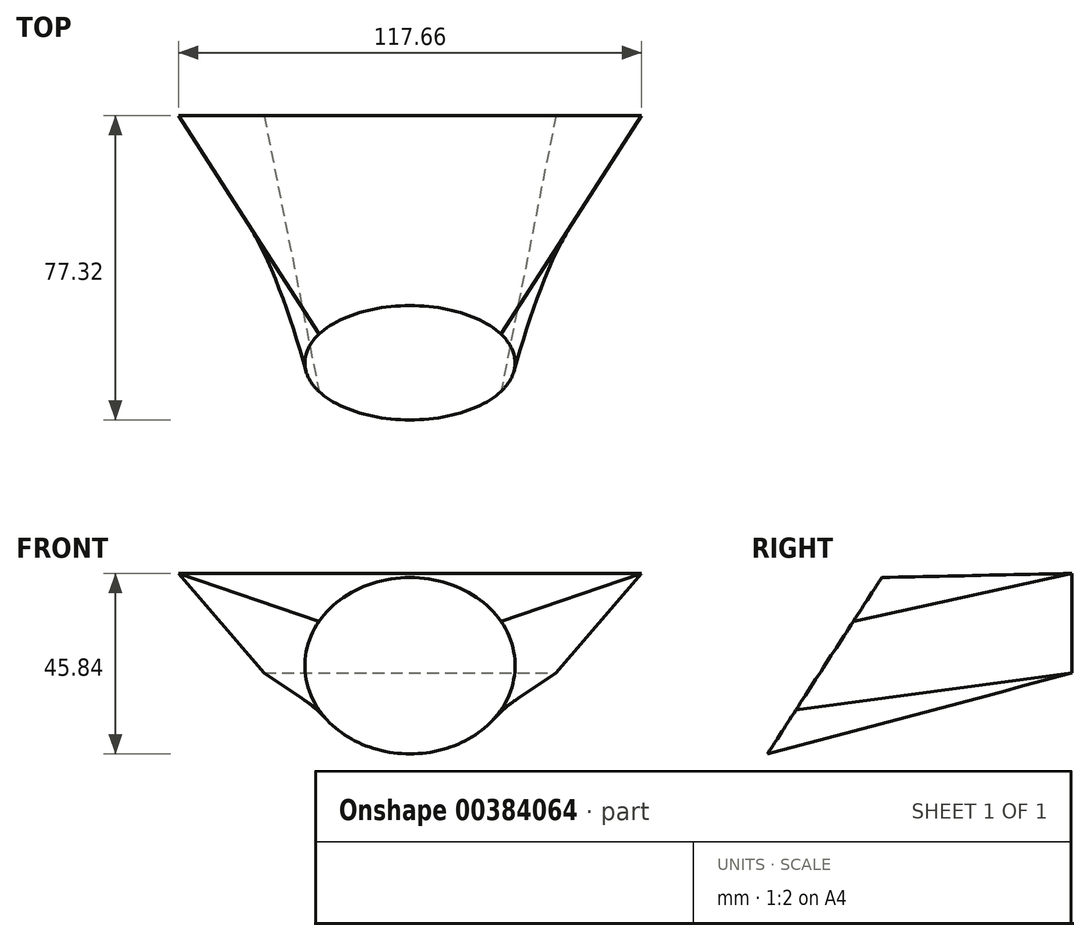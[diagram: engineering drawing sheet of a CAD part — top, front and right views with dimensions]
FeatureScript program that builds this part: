
annotation { "Feature Type Name" : "Feature", "Feature Type Description" : "" }
export const myFeature = defineFeature(function(context is Context, id is Id, definition is map)
    precondition{}
    {
        {
            var Q0;
            Q0=qCreatedBy(makeId("Front.planeOp"),FACE);
            var sketch = newSketch(context, id + "F0", { "sketchPlane" : qUnion([Q0])});
            skLineSegment(sketch, "E0", {"start": v(0, 13.28) * mm, "end": v(-58.83, 13.28) * mm});
            skLineSegment(sketch, "E1", {"start": v(-58.83, 13.28) * mm, "end": v(-37.06, -12.04) * mm});
            skLineSegment(sketch, "E2", {"start": v(-37.06, -12.04) * mm, "end": v(0, -12.04) * mm});
            skPoint(sketch, "E3.endSnap0", {"position": v(-2.33, -12.04) * mm});
            skLineSegment(sketch, "E4", {"start": v(0, -12.04) * mm, "end": v(-37.06, -12.04) * mm});
            skPoint(sketch, "E5.end.orphan", {"position": v(32.4, -12.04) * mm});
            skLineSegment(sketch, "E6.MirrorCS", {"start": v(0, -12.04) * mm, "end": v(37.06, -12.04) * mm});
            skLineSegment(sketch, "E7.MirrorCS", {"start": v(58.83, 13.28) * mm, "end": v(37.06, -12.04) * mm});
            skLineSegment(sketch, "E8.MirrorCS", {"start": v(0, 13.28) * mm, "end": v(58.83, 13.28) * mm});
            skSolve(sketch);
        }
        {
            var Q0;
            Q0=qCreatedBy(makeId("Right.planeOp"),FACE);
            var sketch = newSketch(context, id + "F1", { "sketchPlane" : qUnion([Q0])});
            skLineSegment(sketch, "E9", {"start": v(0, 0) * mm, "end": v(-46.97, -72.49) * mm});
            skLineSegment(sketch, "E10", {"start": v(-46.97, -72.49) * mm, "end": v(-86.57, -46.83) * mm});
            skLineSegment(sketch, "E11", {"start": v(-86.57, -46.83) * mm, "end": v(-40.66, 24.02) * mm});
            skLineSegment(sketch, "E12", {"start": v(-40.66, 24.02) * mm, "end": v(0, 0) * mm});
            skSolve(sketch);
        }
        {
            var Q0;
            Q0=qCreatedBy(makeId("Front.planeOp"),FACE);
            var Q1;
            Q1=sQuery(id+"F1.wireOp",EDGE,"E11");
            cPlane(context, id + "F2", {"entities" : qUnion([Q0, Q1]), "cplaneType" : CPlaneType.LINE_ANGLE, "offset" : 25.4 * mm, "angle" : 0 * degree, "width" : 152.4 * mm, "height" : 152.4 * mm});
        }
        {
            var Q0;
            Q0=qCreatedBy(id+"F2.planeOp",FACE);
            var sketch = newSketch(context, id + "F3", { "sketchPlane" : qUnion([Q0])});
            skCircle(sketch, "E13", {"center": v(0, -42.66) * mm, "radius": 26.7 * mm});
            skSolve(sketch);
        }
        {
            var Q0;
            Q0=makeQuery(id+"F0.imprint","IMPRINT",FACE,{"disambiguationData":[TD([[makeQuery(id+"F0.imprint","IMPRINT",EDGE,{"derivedFrom":sQuery(id+"F0.wireOp",EDGE,"E0")}),1.0]])]});
            var Q1;
            Q1=makeQuery(id+"F3.imprint","IMPRINT",FACE,{"disambiguationData":[TD([[makeQuery(id+"F3.imprint","IMPRINT",EDGE,{"derivedFrom":sQuery(id+"F3.wireOp",EDGE,"E13")}),1.0]])]});
            loft(context, id + "F4", {"sheetProfilesArray" : [{ "sheetProfileEntities" : qUnion([Q0]) }, { "sheetProfileEntities" : qUnion([Q1]) }]});
        }
    });
